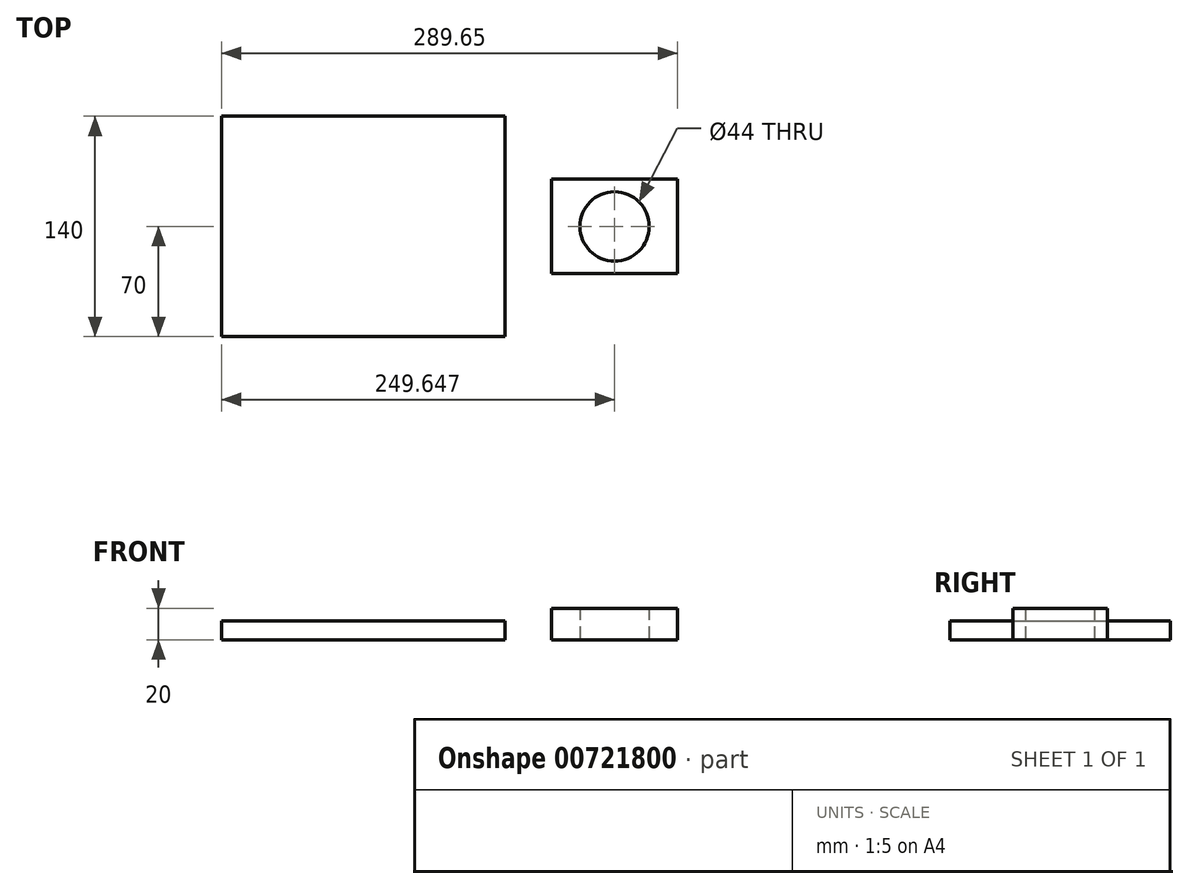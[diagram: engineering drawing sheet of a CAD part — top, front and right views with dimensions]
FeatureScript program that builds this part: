
annotation { "Feature Type Name" : "Feature", "Feature Type Description" : "" }
export const myFeature = defineFeature(function(context is Context, id is Id, definition is map)
    precondition{}
    {
        {
            var Q0;
            Q0=qCreatedBy(makeId("Top.planeOp"),FACE);
            var sketch = newSketch(context, id + "F0", { "sketchPlane" : qUnion([Q0])});
            skLineSegment(sketch, "E0.bottom", {"start": v(90, -70) * mm, "end": v(-90, -70) * mm});
            skLineSegment(sketch, "E0.top", {"start": v(90, 70) * mm, "end": v(-90, 70) * mm});
            skLineSegment(sketch, "E0.left", {"start": v(90, -70) * mm, "end": v(90, 70) * mm});
            skLineSegment(sketch, "E0.right", {"start": v(-90, -70) * mm, "end": v(-90, 70) * mm});
            skPoint(sketch, "E0.middle", {"position": v(0, 0) * mm});
            skSolve(sketch);
        }
        {
            var Q0;
            Q0 = qSketchRegion(id + "F0", true);
            extrude(context, id + "F1", {"entities" : qUnion([Q0]), "depth" : 12 * mm, "offsetDistance" : 25 * mm});
        }
        {
            var Q0;
            Q0=qCreatedBy(makeId("Top.planeOp"),FACE);
            var sketch = newSketch(context, id + "F2", { "sketchPlane" : qUnion([Q0])});
            skCircle(sketch, "E1", {"center": v(159.65, 0) * mm, "radius": 22 * mm});
            skLineSegment(sketch, "E2.bottom", {"start": v(199.65, -30) * mm, "end": v(119.65, -30) * mm});
            skLineSegment(sketch, "E2.top", {"start": v(199.65, 30) * mm, "end": v(119.65, 30) * mm});
            skLineSegment(sketch, "E2.left", {"start": v(199.65, -30) * mm, "end": v(199.65, 30) * mm});
            skLineSegment(sketch, "E2.right", {"start": v(119.65, -30) * mm, "end": v(119.65, 30) * mm});
            skSolve(sketch);
        }
        {
            var Q0;
            Q0 = qSketchRegion(id + "F2", true);
            extrude(context, id + "F3", {"entities" : qUnion([Q0]), "depth" : 20 * mm, "offsetDistance" : 25 * mm});
        }
    });
